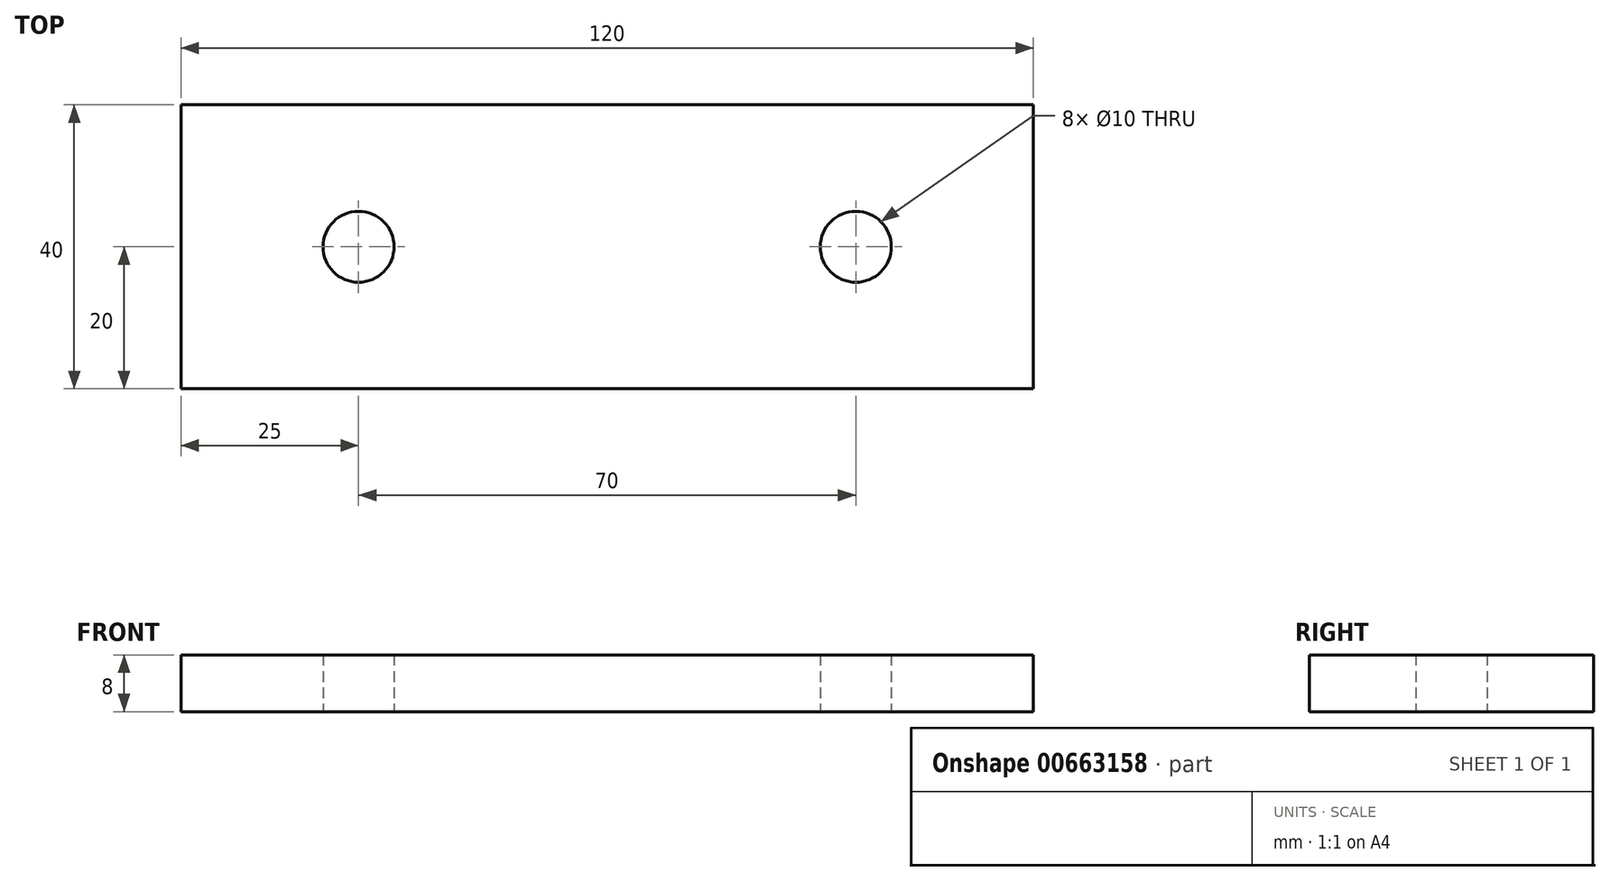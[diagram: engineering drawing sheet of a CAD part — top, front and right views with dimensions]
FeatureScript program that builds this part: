
annotation { "Feature Type Name" : "Feature", "Feature Type Description" : "" }
export const myFeature = defineFeature(function(context is Context, id is Id, definition is map)
    precondition{}
    {
        {
            var Q0;
            Q0=qCreatedBy(makeId("Top.planeOp"),FACE);
            var sketch = newSketch(context, id + "F0", { "sketchPlane" : qUnion([Q0])});
            skLineSegment(sketch, "E0.bottom", {"start": v(60, 20) * mm, "end": v(-60, 20) * mm});
            skLineSegment(sketch, "E0.top", {"start": v(60, -20) * mm, "end": v(-60, -20) * mm});
            skLineSegment(sketch, "E0.left", {"start": v(60, 20) * mm, "end": v(60, -20) * mm});
            skLineSegment(sketch, "E0.right", {"start": v(-60, 20) * mm, "end": v(-60, -20) * mm});
            skPoint(sketch, "E0.middle", {"position": v(0, 0) * mm});
            skCircle(sketch, "E1", {"center": v(-35, 0) * mm, "radius": 5 * mm});
            skCircle(sketch, "E2", {"center": v(35, 0) * mm, "radius": 5 * mm});
            skSolve(sketch);
        }
        {
            var Q0;
            Q0=makeQuery(id+"F0.imprint","IMPRINT",FACE,{"disambiguationData":[TD([[makeQuery(id+"F0.imprint","IMPRINT",EDGE,{"derivedFrom":sQuery(id+"F0.wireOp",EDGE,"E0.bottom")}),1.0]])]});
            extrude(context, id + "F1", {"entities" : qUnion([Q0]), "endBound" : BoundingType.SYMMETRIC, "depth" : 8 * mm, "offsetDistance" : 25 * mm});
        }
    });
